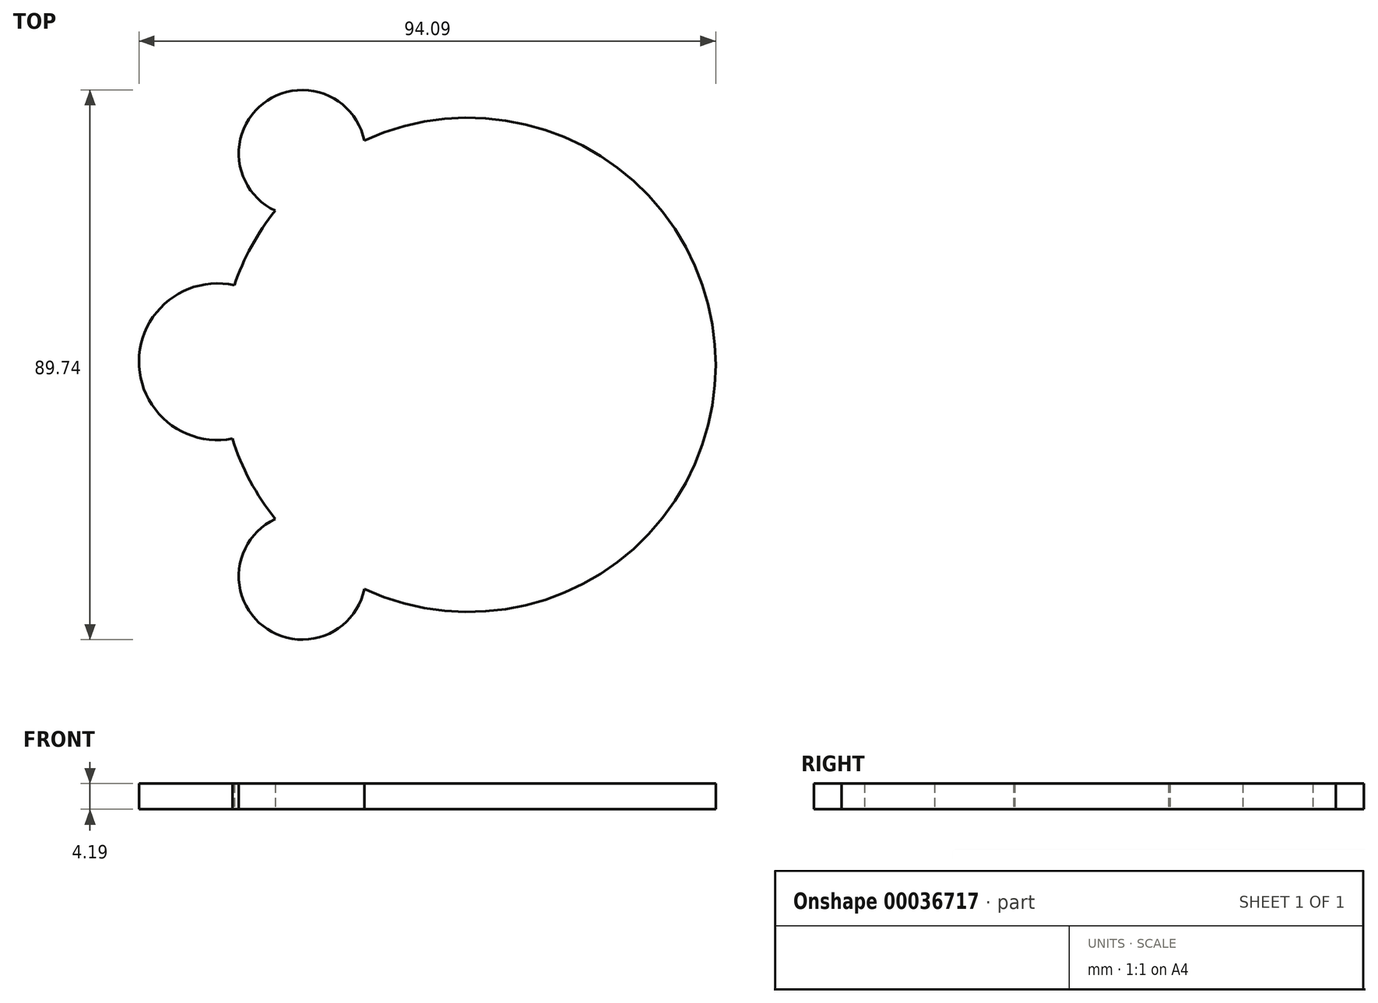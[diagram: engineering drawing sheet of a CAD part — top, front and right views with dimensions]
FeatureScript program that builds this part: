
annotation { "Feature Type Name" : "Feature", "Feature Type Description" : "" }
export const myFeature = defineFeature(function(context is Context, id is Id, definition is map)
    precondition{}
    {
        {
            var Q0;
            Q0=qCreatedBy(makeId("Top.planeOp"),FACE);
            var sketch = newSketch(context, id + "F0", { "sketchPlane" : qUnion([Q0])});
            skArc(sketch, "E0", {"start": v(-31.53, 25.16) * mm, "mid": v(-35.4, 19.36) * mm, "end": v(-38.2, 12.99) * mm});
            skArc(sketch, "E1", {"start": v(-38.2, 12.99) * mm, "mid": v(-53.75, 0.67) * mm, "end": v(-38.5, -12.04) * mm});
            skArc(sketch, "E2", {"start": v(-16.98, 36.6) * mm, "mid": v(-33.5, 42.65) * mm, "end": v(-31.53, 25.16) * mm});
            skArc(sketch, "E3.MirrorCS", {"start": v(-16.98, -36.6) * mm, "mid": v(-33.5, -42.65) * mm, "end": v(-31.53, -25.16) * mm});
            skArc(sketch, "E4.trimOffspring", {"start": v(-38.5, -12.04) * mm, "mid": v(-35.63, -18.92) * mm, "end": v(-31.53, -25.16) * mm});
            skArc(sketch, "E5.trimOffspring", {"start": v(-16.98, -36.6) * mm, "mid": v(40.34, 0) * mm, "end": v(-16.98, 36.6) * mm});
            skSolve(sketch);
        }
        {
            var Q0;
            Q0=makeQuery(id+"F0.imprint","IMPRINT",FACE,{"disambiguationData":[TD([[makeQuery(id+"F0.imprint","IMPRINT",EDGE,{"derivedFrom":sQuery(id+"F0.wireOp",EDGE,"E0")}),1.0]])]});
            extrude(context, id + "F1", {"entities" : qUnion([Q0]), "depth" : 4.2 * mm});
        }
    });
